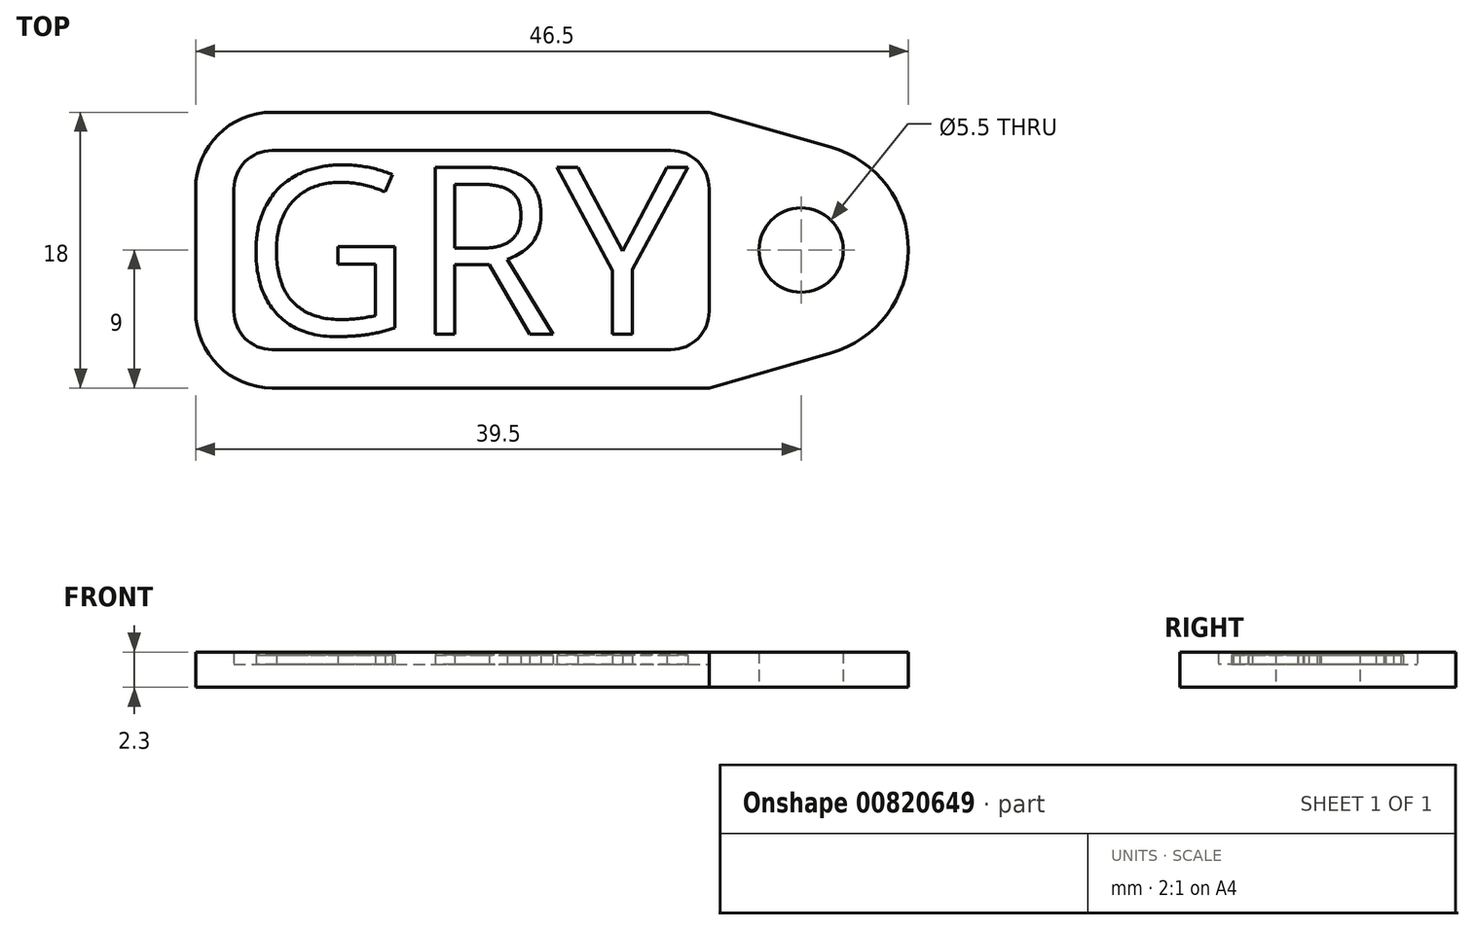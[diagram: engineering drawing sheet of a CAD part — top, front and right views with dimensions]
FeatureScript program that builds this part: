
annotation { "Feature Type Name" : "Feature", "Feature Type Description" : "" }
export const myFeature = defineFeature(function(context is Context, id is Id, definition is map)
    precondition{}
    {
        {
            var Q0;
            Q0=qCreatedBy(makeId("Top.planeOp"),FACE);
            var sketch = newSketch(context, id + "F0", { "sketchPlane" : qUnion([Q0])});
            skLineSegment(sketch, "E0", {"start": v(5, 9) * mm, "end": v(33.5, 9) * mm});
            skLineSegment(sketch, "E1", {"start": v(33.5, 9) * mm, "end": v(41.43, 6.73) * mm});
            skLineSegment(sketch, "E2", {"start": v(41.43, -6.73) * mm, "end": v(33.5, -9) * mm});
            skLineSegment(sketch, "E3", {"start": v(33.5, -9) * mm, "end": v(5, -9) * mm});
            skLineSegment(sketch, "E4", {"start": v(0, -4) * mm, "end": v(0, 4) * mm});
            skPoint(sketch, "E5.visualSharp", {"position": v(64.92, 0) * mm});
            skArc(sketch, "E5.filletArc", {"start": v(41.43, -6.73) * mm, "mid": v(46.5, 0) * mm, "end": v(41.43, 6.73) * mm});
            skPoint(sketch, "E6.visualSharp", {"position": v(0, 9) * mm});
            skArc(sketch, "E6.filletArc", {"start": v(5, 9) * mm, "mid": v(1.46, 7.54) * mm, "end": v(0, 4) * mm});
            skPoint(sketch, "E7.visualSharp", {"position": v(0, -9) * mm});
            skArc(sketch, "E7.filletArc", {"start": v(0, -4) * mm, "mid": v(1.46, -7.54) * mm, "end": v(5, -9) * mm});
            skSolve(sketch);
        }
        {
            var Q0;
            Q0=makeQuery(id+"F0.imprint","IMPRINT",FACE,{"disambiguationData":[TD([[makeQuery(id+"F0.imprint","IMPRINT",EDGE,{"derivedFrom":sQuery(id+"F0.wireOp",EDGE,"E0")}),-1.0]])]});
            extrude(context, id + "F1", {"entities" : qUnion([Q0]), "depth" : 1.5 * mm, "offsetDistance" : 25 * mm});
        }
        {
            var Q0;
            Q0=sQuery(id+"F0.wireOp",VERTEX,"E5.filletArc.center");
            var Q1;
            Q1=makeQuery(id+"F1.opExtrude","SWEPT_BODY",BODY,{"disambiguationData":[OSD([sQuery(id+"F0.wireOp",EDGE,"E0"),sQuery(id+"F0.wireOp",EDGE,"E1"),sQuery(id+"F0.wireOp",EDGE,"E2"),sQuery(id+"F0.wireOp",EDGE,"E3"),sQuery(id+"F0.wireOp",EDGE,"E4"),sQuery(id+"F0.wireOp",EDGE,"E5.filletArc"),sQuery(id+"F0.wireOp",EDGE,"E6.filletArc"),sQuery(id+"F0.wireOp",EDGE,"E7.filletArc")])]});
            hole(context, id + "F2", {"style" : HoleStyle.SIMPLE, "endStyle" : HoleEndStyle.THROUGH, "oppositeDirection" : true, "holeDiameter" : 5.5 * mm, "majorDiameter" : 5 * mm, "isTappedThrough" : true, "tappedDepth" : 12 * mm, "tapClearance" : 3, "locations" : qUnion([Q0]), "scope" : qUnion([Q1])});
        }
        {
            var Q0;
            Q0=makeQuery(id+"F1.opExtrude","CAP_FACE",FACE,{"disambiguationData":[OSD([sQuery(id+"F0.wireOp",EDGE,"E0"),sQuery(id+"F0.wireOp",EDGE,"E1"),sQuery(id+"F0.wireOp",EDGE,"E2"),sQuery(id+"F0.wireOp",EDGE,"E3"),sQuery(id+"F0.wireOp",EDGE,"E4"),sQuery(id+"F0.wireOp",EDGE,"E5.filletArc"),sQuery(id+"F0.wireOp",EDGE,"E6.filletArc"),sQuery(id+"F0.wireOp",EDGE,"E7.filletArc")])],"isStart":false});
            var sketch = newSketch(context, id + "F3", { "sketchPlane" : qUnion([Q0])});
            skLineSegment(sketch, "E8", {"start": v(2.5, 4) * mm, "end": v(2.5, -4) * mm});
            skLineSegment(sketch, "E9", {"start": v(5, -6.5) * mm, "end": v(31, -6.5) * mm});
            skLineSegment(sketch, "E10", {"start": v(33.5, -4) * mm, "end": v(33.5, 4) * mm});
            skLineSegment(sketch, "E11", {"start": v(31, 6.5) * mm, "end": v(5, 6.5) * mm});
            skPoint(sketch, "E12.visualSharp", {"position": v(2.5, 6.5) * mm});
            skArc(sketch, "E12.filletArc", {"start": v(5, 6.5) * mm, "mid": v(3.23, 5.77) * mm, "end": v(2.5, 4) * mm});
            skPoint(sketch, "E13.visualSharp", {"position": v(2.5, -6.5) * mm});
            skArc(sketch, "E13.filletArc", {"start": v(2.5, -4) * mm, "mid": v(3.23, -5.77) * mm, "end": v(5, -6.5) * mm});
            skPoint(sketch, "E14.visualSharp", {"position": v(33.5, -6.5) * mm});
            skArc(sketch, "E14.filletArc", {"start": v(31, -6.5) * mm, "mid": v(32.77, -5.77) * mm, "end": v(33.5, -4) * mm});
            skPoint(sketch, "E15.visualSharp", {"position": v(33.5, 6.5) * mm});
            skArc(sketch, "E15.filletArc", {"start": v(33.5, 4) * mm, "mid": v(32.77, 5.77) * mm, "end": v(31, 6.5) * mm});
            skText(sketch, "E16", { "text": "GRY", "fontName": "OpenSans-Regular.ttf"});
            const initialGuessF3  = {"E16": [0.003, -0.0055, 1, 0, 0.011]};
            skSetInitialGuess(sketch, initialGuessF3);
            skSolve(sketch);
        }
        {
            var Q0;
            Q0=makeQuery(id+"F3.imprint","IMPRINT",FACE,{"disambiguationData":[TD([[makeQuery(id+"F3.imprint","IMPRINT",EDGE,{"derivedFrom":sQuery(id+"F3.wireOp",EDGE,"E16.sketch_text.stroke-0")}),-1.0]])]});
            var Q1;
            Q1=makeQuery(id+"F3.imprint","IMPRINT",FACE,{"disambiguationData":[TD([[makeQuery(id+"F3.imprint","IMPRINT",EDGE,{"derivedFrom":sQuery(id+"F3.wireOp",EDGE,"E16.sketch_text.stroke-20")}),-1.0]])]});
            var Q2;
            Q2=makeQuery(id+"F3.imprint","IMPRINT",FACE,{"disambiguationData":[TD([[makeQuery(id+"F3.imprint","IMPRINT",EDGE,{"derivedFrom":sQuery(id+"F3.wireOp",EDGE,"E16.sketch_text.stroke-38")}),-1.0]])]});
            extrude(context, id + "F4", {"entities" : qUnion([Q0, Q1, Q2]), "operationType" : NewBodyOperationType.ADD, "depth" : .6 * mm, "offsetDistance" : 25 * mm});
        }
        {
            var Q0;
            Q0=makeQuery(id+"F3.imprint","IMPRINT",FACE,{"disambiguationData":[TD([[makeQuery(id+"F3.imprint","IMPRINT",EDGE,{"derivedFrom":sQuery(id+"F3.wireOp",EDGE,"E8")}),-1.0]])]});
            extrude(context, id + "F5", {"entities" : qUnion([Q0]), "operationType" : NewBodyOperationType.ADD, "depth" : .8 * mm, "offsetDistance" : 25 * mm});
        }
    });
